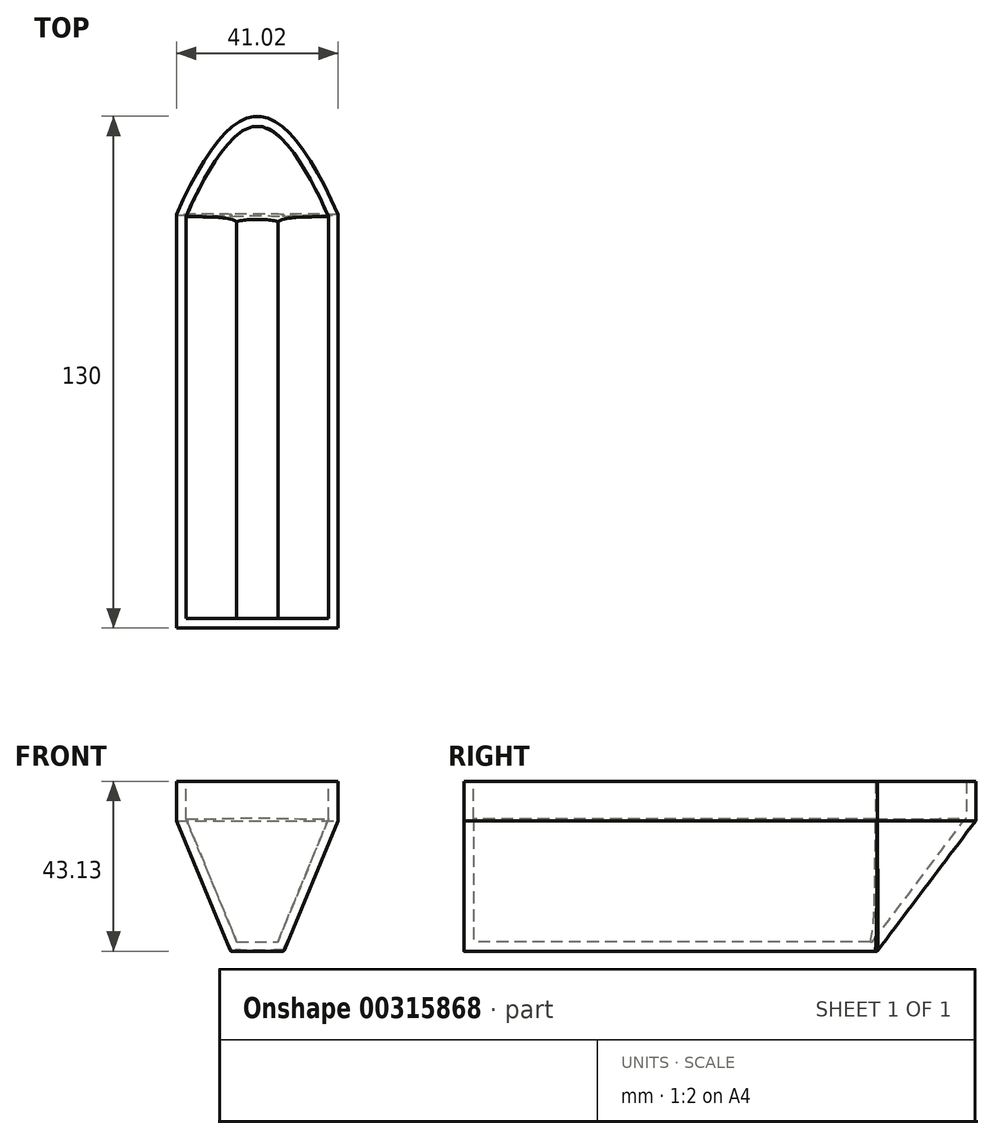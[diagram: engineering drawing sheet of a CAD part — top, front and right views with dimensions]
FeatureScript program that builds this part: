
annotation { "Feature Type Name" : "Feature", "Feature Type Description" : "" }
export const myFeature = defineFeature(function(context is Context, id is Id, definition is map)
    precondition{}
    {
        {
            var Q0;
            Q0=qCreatedBy(makeId("Top.planeOp"),FACE);
            cPlane(context, id + "F0", {"entities" : qUnion([Q0]), "cplaneType" : CPlaneType.OFFSET, "offset" : 33.12 * mm, "width" : 150 * mm, "height" : 150 * mm});
        }
        {
            var Q0;
            Q0=qCreatedBy(id+"F0.planeOp",FACE);
            var sketch = newSketch(context, id + "F1", { "sketchPlane" : qUnion([Q0])});
            skLineSegment(sketch, "E0", {"start": v(-20.5, 0) * mm, "end": v(-20.5, -105) * mm});
            skLineSegment(sketch, "E1", {"start": v(-20.5, -105) * mm, "end": v(20.5, -105) * mm});
            skLineSegment(sketch, "E2", {"start": v(20.5, -105) * mm, "end": v(20.5, 0) * mm});
            skPoint(sketch, "E3", {"position": v(0, 25) * mm});
            skFitSpline(sketch, "E4", {"points": [v(-20.5, 0) * mm, v(0, 25) * mm, v(20.5, 0) * mm], "startDerivative": vector(39, 90) * mm, "endDerivative": vector(39, -90) * mm});
            skSolve(sketch);
        }
        {
            var Q0;
            Q0=qCreatedBy(makeId("Top.planeOp"),FACE);
            var sketch = newSketch(context, id + "F2", { "sketchPlane" : qUnion([Q0])});
            skLineSegment(sketch, "E5", {"start": v(6.83, 0) * mm, "end": v(6.83, -105) * mm});
            skLineSegment(sketch, "E6", {"start": v(6.83, -105) * mm, "end": v(-6.83, -105) * mm});
            skLineSegment(sketch, "E7", {"start": v(-6.83, -105) * mm, "end": v(-6.83, 0) * mm});
            skLineSegment(sketch, "E8", {"start": v(-6.83, 0) * mm, "end": v(6.83, 0) * mm});
            skSolve(sketch);
        }
        {
            var Q0;
            Q0=makeQuery(id+"F1.imprint","IMPRINT",FACE,{"disambiguationData":[TD([[makeQuery(id+"F1.imprint","IMPRINT",EDGE,{"derivedFrom":sQuery(id+"F1.wireOp",EDGE,"E0")}),1.0]])]});
            var Q1;
            Q1=makeQuery(id+"F2.imprint","IMPRINT",FACE,{"disambiguationData":[TD([[makeQuery(id+"F2.imprint","IMPRINT",EDGE,{"derivedFrom":sQuery(id+"F2.wireOp",EDGE,"E5")}),-1.0]])]});
            loft(context, id + "F3", {"sheetProfilesArray" : [{ "sheetProfileEntities" : qUnion([Q0]) }, { "sheetProfileEntities" : qUnion([Q1]) }]});
        }
        {
            var Q0;
            Q0=makeQuery(id+"F3.opLoft","CAP_FACE",FACE,{"disambiguationData":[OSD([makeQuery(id+"F1.imprint","IMPRINT",FACE,{"disambiguationData":[TD([[makeQuery(id+"F1.imprint","IMPRINT",EDGE,{"derivedFrom":sQuery(id+"F1.wireOp",EDGE,"E0")}),1.0]])]})])],"isStart":true});
            extrude(context, id + "F4", {"entities" : qUnion([Q0]), "operationType" : NewBodyOperationType.ADD, "depth" : 10 * mm});
        }
        {
            var Q0;
            Q0=makeQuery(id+"F4.opExtrude","CAP_FACE",FACE,{"disambiguationData":[OSD([makeQuery(id+"F1.imprint","IMPRINT",FACE,{"disambiguationData":[TD([[makeQuery(id+"F1.imprint","IMPRINT",EDGE,{"derivedFrom":sQuery(id+"F1.wireOp",EDGE,"E0")}),1.0]])]})])],"isStart":false});
            shell(context, id + "F5", {"entities" : qUnion([Q0]), "thickness" : 2.4 * mm});
        }
        {
            var Q0;
            Q0=makeQuery(id+"F3.opLoft","MID_CAP_EDGE",EDGE,{"disambiguationData":[OSD([sQuery(id+"F2.wireOp",EDGE,"E6"),sQuery(id+"F2.wireOp",EDGE,"E7"),sQuery(id+"F2.wireOp",EDGE,"E8")])],"capPos":1.0});
            var Q1;
            Q1=makeQuery(id+"F3.opLoft","MID_CAP_EDGE",EDGE,{"disambiguationData":[OSD([sQuery(id+"F2.wireOp",EDGE,"E5"),sQuery(id+"F2.wireOp",EDGE,"E6"),sQuery(id+"F2.wireOp",EDGE,"E8")])],"capPos":1.0});
            var Q2;
            Q2=makeQuery(id+"F3.opLoft","MID_CAP_EDGE",EDGE,{"disambiguationData":[OSD([sQuery(id+"F2.wireOp",EDGE,"E5"),sQuery(id+"F2.wireOp",EDGE,"E7"),sQuery(id+"F2.wireOp",EDGE,"E8")])],"capPos":1.0});
            var Q3;
            Q3=makeQuery(id+"F3.opLoft","SWEPT_EDGE",EDGE,{"disambiguationData":[OSD([sQuery(id+"F1.wireOp",EDGE,"E2"),sQuery(id+"F1.wireOp",EDGE,"E4"),sQuery(id+"F2.wireOp",EDGE,"E5"),sQuery(id+"F2.wireOp",EDGE,"E8")])]});
            var Q4;
            Q4=makeQuery(id+"F3.opLoft","SWEPT_EDGE",EDGE,{"disambiguationData":[OSD([sQuery(id+"F1.wireOp",EDGE,"E0"),sQuery(id+"F1.wireOp",EDGE,"E4"),sQuery(id+"F2.wireOp",EDGE,"E7"),sQuery(id+"F2.wireOp",EDGE,"E8")])]});
            fillet(context, id + "F6", {"entities" : qUnion([Q0, Q1, Q2, Q3, Q4]), "radius" : .5 * mm, "tangentPropagation" : true, "allowEdgeOverflow" : false});
        }
    });
